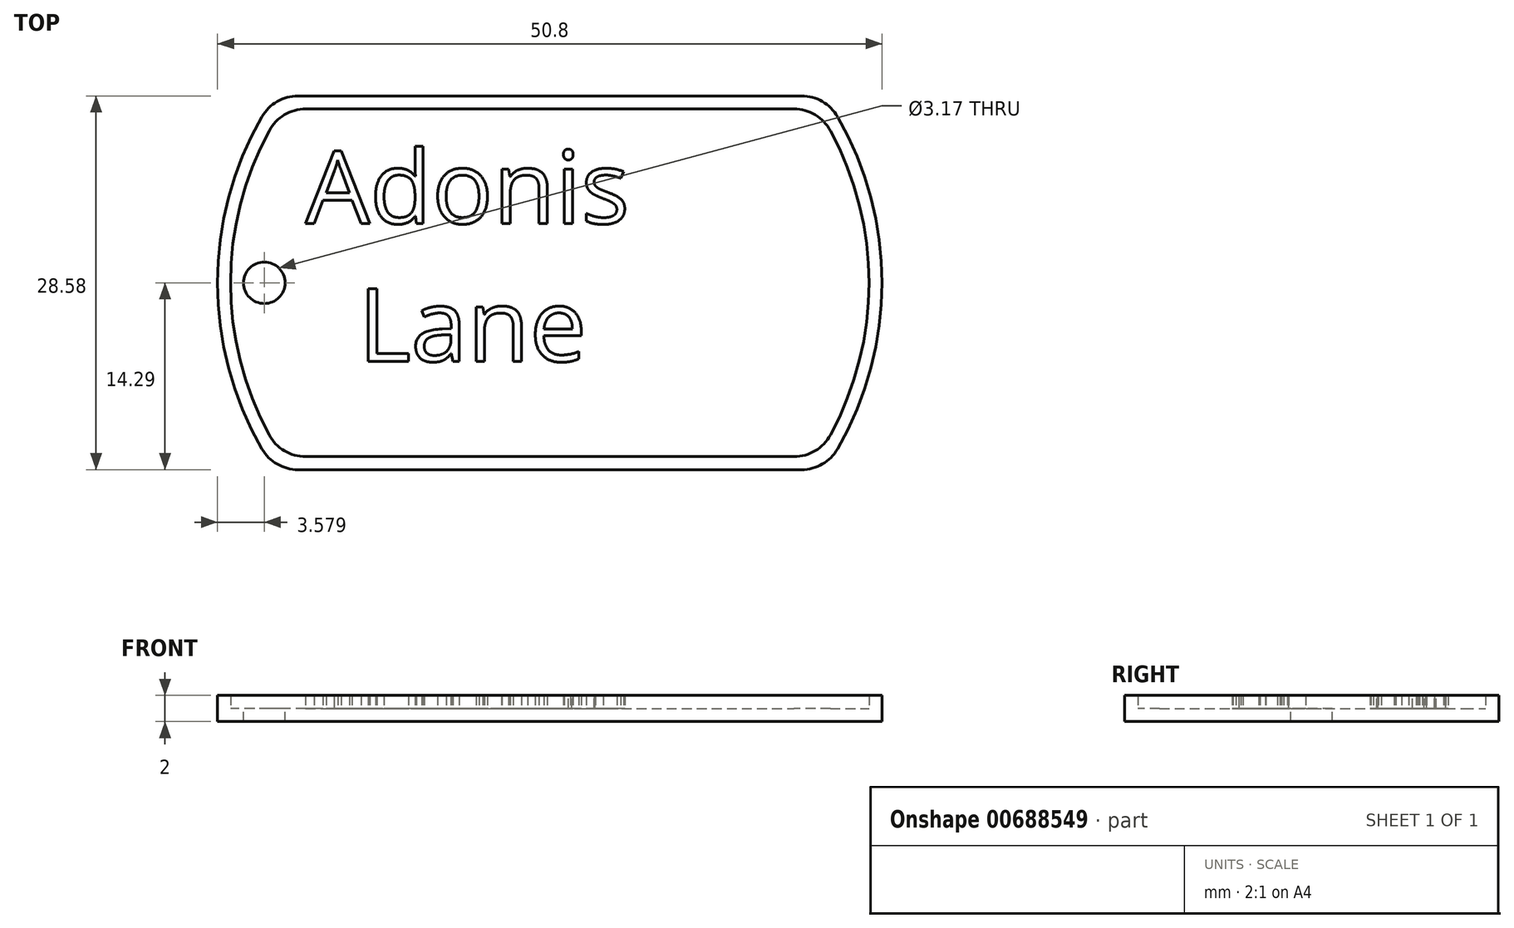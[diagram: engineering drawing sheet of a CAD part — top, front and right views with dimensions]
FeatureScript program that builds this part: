
annotation { "Feature Type Name" : "Feature", "Feature Type Description" : "" }
export const myFeature = defineFeature(function(context is Context, id is Id, definition is map)
    precondition{}
    {
        {
            var Q0;
            Q0=qCreatedBy(makeId("Top.planeOp"),FACE);
            var sketch = newSketch(context, id + "F0", { "sketchPlane" : qUnion([Q0])});
            skArc(sketch, "E0", {"start": v(-22, 12.7) * mm, "mid": v(-25.4, 0) * mm, "end": v(-22, -12.7) * mm});
            skLineSegment(sketch, "E1.top", {"start": v(-19.25, -14.29) * mm, "end": v(19.25, -14.29) * mm});
            skArc(sketch, "E2.trimOffspring", {"start": v(22, -12.7) * mm, "mid": v(25.4, 0) * mm, "end": v(22, 12.7) * mm});
            skLineSegment(sketch, "E3", {"start": v(-19.25, 14.29) * mm, "end": v(19.25, 14.29) * mm});
            skPoint(sketch, "E4.visualSharp", {"position": v(-21, 14.29) * mm});
            skArc(sketch, "E4.filletArc", {"start": v(-19.25, 14.29) * mm, "mid": v(-20.83, 13.86) * mm, "end": v(-22, 12.7) * mm});
            skPoint(sketch, "E5.visualSharp", {"position": v(21, 14.29) * mm});
            skArc(sketch, "E5.filletArc", {"start": v(22, 12.7) * mm, "mid": v(20.83, 13.86) * mm, "end": v(19.25, 14.29) * mm});
            skPoint(sketch, "E6.visualSharp", {"position": v(21, -14.29) * mm});
            skArc(sketch, "E6.filletArc", {"start": v(19.25, -14.29) * mm, "mid": v(20.83, -13.86) * mm, "end": v(22, -12.7) * mm});
            skPoint(sketch, "E7.visualSharp", {"position": v(-21, -14.29) * mm});
            skArc(sketch, "E7.filletArc", {"start": v(-22, -12.7) * mm, "mid": v(-20.83, -13.86) * mm, "end": v(-19.25, -14.29) * mm});
            skSolve(sketch);
        }
        {
            var Q0;
            Q0=makeQuery(id+"F0.imprint","IMPRINT",FACE,{"disambiguationData":[TD([[makeQuery(id+"F0.imprint","IMPRINT",EDGE,{"derivedFrom":sQuery(id+"F0.wireOp",EDGE,"E0")}),1.0]])]});
            extrude(context, id + "F1", {"entities" : qUnion([Q0]), "depth" : 1 * mm, "offsetDistance" : 25.4 * mm});
        }
        {
            var Q0;
            Q0=makeQuery(id+"F1.opExtrude","CAP_FACE",FACE,{"disambiguationData":[OSD([sQuery(id+"F0.wireOp",EDGE,"E0"),sQuery(id+"F0.wireOp",EDGE,"E1.top"),sQuery(id+"F0.wireOp",EDGE,"E2.trimOffspring"),sQuery(id+"F0.wireOp",EDGE,"E3"),sQuery(id+"F0.wireOp",EDGE,"E4.filletArc"),sQuery(id+"F0.wireOp",EDGE,"E5.filletArc"),sQuery(id+"F0.wireOp",EDGE,"E6.filletArc"),sQuery(id+"F0.wireOp",EDGE,"E7.filletArc")])],"isStart":false});
            var sketch = newSketch(context, id + "F2", { "sketchPlane" : qUnion([Q0])});
            skLineSegment(sketch, "E8.0", {"start": v(-18.66, 13.29) * mm, "end": v(18.66, 13.29) * mm});
            skArc(sketch, "E8.1", {"start": v(-21.45, 11.63) * mm, "mid": v(-24.4, 0) * mm, "end": v(-21.45, -11.63) * mm});
            skLineSegment(sketch, "E8.2", {"start": v(-18.66, -13.29) * mm, "end": v(18.66, -13.29) * mm});
            skArc(sketch, "E8.3", {"start": v(21.45, -11.63) * mm, "mid": v(24.4, 0) * mm, "end": v(21.45, 11.63) * mm});
            skPoint(sketch, "E9.visualSharp", {"position": v(-20.46, 13.29) * mm});
            skArc(sketch, "E9.filletArc", {"start": v(-18.66, 13.29) * mm, "mid": v(-20.29, 12.84) * mm, "end": v(-21.45, 11.63) * mm});
            skPoint(sketch, "E10.visualSharp", {"position": v(20.46, 13.29) * mm});
            skArc(sketch, "E10.filletArc", {"start": v(21.45, 11.63) * mm, "mid": v(20.29, 12.84) * mm, "end": v(18.66, 13.29) * mm});
            skPoint(sketch, "E11.visualSharp", {"position": v(20.46, -13.29) * mm});
            skArc(sketch, "E11.filletArc", {"start": v(18.66, -13.29) * mm, "mid": v(20.29, -12.84) * mm, "end": v(21.45, -11.63) * mm});
            skPoint(sketch, "E12.visualSharp", {"position": v(-20.46, -13.29) * mm});
            skArc(sketch, "E12.filletArc", {"start": v(-21.45, -11.63) * mm, "mid": v(-20.29, -12.84) * mm, "end": v(-18.66, -13.29) * mm});
            skLineSegment(sketch, "E13.0", {"start": v(-19.25, 14.29) * mm, "end": v(19.25, 14.29) * mm});
            skArc(sketch, "E13.1", {"start": v(-22, 12.7) * mm, "mid": v(-25.4, 0) * mm, "end": v(-22, -12.7) * mm});
            skLineSegment(sketch, "E13.2", {"start": v(-19.25, -14.29) * mm, "end": v(19.25, -14.29) * mm});
            skArc(sketch, "E13.3", {"start": v(22, -12.7) * mm, "mid": v(25.4, 0) * mm, "end": v(22, 12.7) * mm});
            skPoint(sketch, "E14.visualSharp", {"position": v(-21, -14.29) * mm});
            skArc(sketch, "E14.filletArc", {"start": v(-22, -12.7) * mm, "mid": v(-20.83, -13.86) * mm, "end": v(-19.25, -14.29) * mm});
            skPoint(sketch, "E15.visualSharp", {"position": v(21, -14.29) * mm});
            skArc(sketch, "E15.filletArc", {"start": v(19.25, -14.29) * mm, "mid": v(20.83, -13.86) * mm, "end": v(22, -12.7) * mm});
            skPoint(sketch, "E16.visualSharp", {"position": v(21, 14.29) * mm});
            skArc(sketch, "E16.filletArc", {"start": v(22, 12.7) * mm, "mid": v(20.83, 13.86) * mm, "end": v(19.25, 14.29) * mm});
            skPoint(sketch, "E17.visualSharp", {"position": v(-21, 14.29) * mm});
            skArc(sketch, "E17.filletArc", {"start": v(-19.25, 14.29) * mm, "mid": v(-20.83, 13.86) * mm, "end": v(-22, 12.7) * mm});
            skSolve(sketch);
        }
        {
            var Q0;
            Q0=makeQuery(id+"F2.imprint","IMPRINT",FACE,{"disambiguationData":[TD([[makeQuery(id+"F2.imprint","IMPRINT",EDGE,{"derivedFrom":sQuery(id+"F2.wireOp",EDGE,"E8.0")}),1.0]])]});
            extrude(context, id + "F3", {"entities" : qUnion([Q0]), "operationType" : NewBodyOperationType.ADD, "depth" : 1 * mm, "offsetDistance" : 25.4 * mm});
        }
        {
            var Q0;
            Q0=makeQuery(id+"F1.opExtrude","CAP_FACE",FACE,{"disambiguationData":[OSD([sQuery(id+"F0.wireOp",EDGE,"E0"),sQuery(id+"F0.wireOp",EDGE,"E1.top"),sQuery(id+"F0.wireOp",EDGE,"E2.trimOffspring"),sQuery(id+"F0.wireOp",EDGE,"E3"),sQuery(id+"F0.wireOp",EDGE,"E4.filletArc"),sQuery(id+"F0.wireOp",EDGE,"E5.filletArc"),sQuery(id+"F0.wireOp",EDGE,"E6.filletArc"),sQuery(id+"F0.wireOp",EDGE,"E7.filletArc")])],"isStart":false});
            var sketch = newSketch(context, id + "F4", { "sketchPlane" : qUnion([Q0])});
            skCircle(sketch, "E18", {"center": v(-21.82, 0) * mm, "radius": 1.59 * mm});
            skSolve(sketch);
        }
        {
            var Q0;
            Q0=makeQuery(id+"F4.imprint","IMPRINT",FACE,{"disambiguationData":[TD([[makeQuery(id+"F4.imprint","IMPRINT",EDGE,{"derivedFrom":sQuery(id+"F4.wireOp",EDGE,"E18")}),1.0]])]});
            extrude(context, id + "F5", {"entities" : qUnion([Q0]), "operationType" : NewBodyOperationType.REMOVE, "oppositeDirection" : true, "depth" : 1 * mm, "offsetDistance" : 25.4 * mm});
        }
        {
            var Q0;
            Q0=makeQuery(id+"F1.opExtrude","CAP_FACE",FACE,{"disambiguationData":[OSD([sQuery(id+"F0.wireOp",EDGE,"E0"),sQuery(id+"F0.wireOp",EDGE,"E1.top"),sQuery(id+"F0.wireOp",EDGE,"E2.trimOffspring"),sQuery(id+"F0.wireOp",EDGE,"E3"),sQuery(id+"F0.wireOp",EDGE,"E4.filletArc"),sQuery(id+"F0.wireOp",EDGE,"E5.filletArc"),sQuery(id+"F0.wireOp",EDGE,"E6.filletArc"),sQuery(id+"F0.wireOp",EDGE,"E7.filletArc")])],"isStart":false});
            var sketch = newSketch(context, id + "F6", { "sketchPlane" : qUnion([Q0])});
            skText(sketch, "E19", { "text": "Adonis\n  Lane", "fontName": "OpenSans-Regular.ttf"});
            const initialGuessF6  = {"E19": [-0.01866, 0.00454, 1, 0, 0.00558]};
            skSetInitialGuess(sketch, initialGuessF6);
            skSolve(sketch);
        }
        {
            var Q0;
            Q0 = qSketchRegion(id + "F6", true);
            extrude(context, id + "F7", {"entities" : qUnion([Q0]), "operationType" : NewBodyOperationType.ADD, "depth" : 1 * mm, "offsetDistance" : 25.4 * mm});
        }
    });
